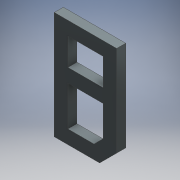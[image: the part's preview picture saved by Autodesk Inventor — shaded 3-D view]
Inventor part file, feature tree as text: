
AUTODESK INVENTOR PART (.ipt)
format: ipt  version: 2016 (Build 200138000, 138)  size: 129,024 bytes
history: native  units: mm
features: extrude x1, sketch x1
ambient origin geometry x8: Origin, YZ Plane, XZ Plane, XY Plane, X Axis, Y Axis, Z Axis, Center Point
bodies: Body1 (feature_tree)
feature tree (2):
  extrude  "Extrusion2"  Depth=82.5mm
  sketch  "Sketch1"  dims[d1=142.5mm d3=82.5mm d4=60.0mm d5=135.0deg d6=120.0mm d8=18.0mm d9=18.0mm d10=18.0mm d11=18.0mm d15=88.5mm d16=18.0mm d17=18.0mm d18=18.0mm d19=18.0mm d20=18.0mm d21=18.0mm d22=12.0mm d23=0.0mm]
